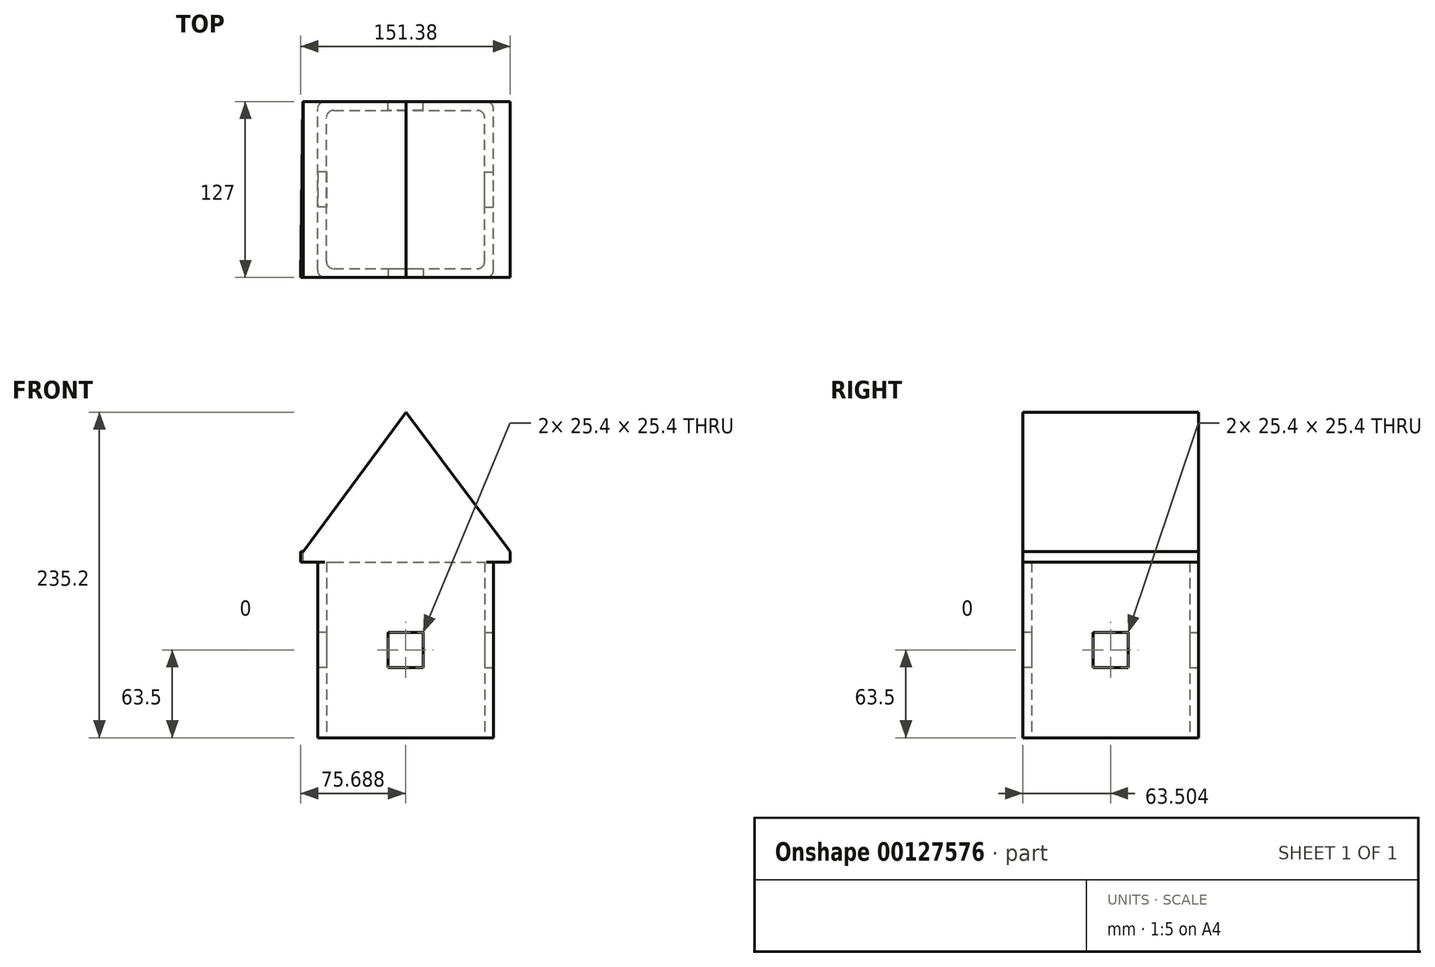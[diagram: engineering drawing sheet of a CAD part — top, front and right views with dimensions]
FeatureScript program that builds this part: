
annotation { "Feature Type Name" : "Feature", "Feature Type Description" : "" }
export const myFeature = defineFeature(function(context is Context, id is Id, definition is map)
    precondition{}
    {
        {
            var Q0;
            Q0=qCreatedBy(makeId("Top.planeOp"),FACE);
            var sketch = newSketch(context, id + "F0", { "sketchPlane" : qUnion([Q0])});
            skLineSegment(sketch, "E0.bottom", {"start": v(-63.96, -29.64) * mm, "end": v(63.04, -29.64) * mm});
            skLineSegment(sketch, "E0.top", {"start": v(-63.96, 97.36) * mm, "end": v(63.04, 97.36) * mm});
            skLineSegment(sketch, "E0.left", {"start": v(-63.96, -29.64) * mm, "end": v(-63.96, 97.36) * mm});
            skLineSegment(sketch, "E0.right", {"start": v(63.04, -29.64) * mm, "end": v(63.04, 97.36) * mm});
            skLineSegment(sketch, "E1.0", {"start": v(-57.61, 91.01) * mm, "end": v(56.69, 91.01) * mm});
            skLineSegment(sketch, "E1.1", {"start": v(-57.61, -23.29) * mm, "end": v(-57.61, 91.01) * mm});
            skLineSegment(sketch, "E1.2", {"start": v(-57.61, -23.29) * mm, "end": v(56.69, -23.29) * mm});
            skLineSegment(sketch, "E1.3", {"start": v(56.69, -23.29) * mm, "end": v(56.69, 91.01) * mm});
            skSolve(sketch);
        }
        {
            var Q0;
            Q0=makeQuery(id+"F0.imprint","IMPRINT",FACE,{"disambiguationData":[TD([[makeQuery(id+"F0.imprint","IMPRINT",EDGE,{"derivedFrom":sQuery(id+"F0.wireOp",EDGE,"E0.bottom")}),1.0]])]});
            extrude(context, id + "F1", {"entities" : qUnion([Q0]), "depth" : 127 * mm});
        }
        {
            var Q0;
            Q0=makeQuery(id+"F1.opExtrude","SWEPT_FACE",FACE,{"disambiguationData":[OSD([sQuery(id+"F0.wireOp",EDGE,"E0.right")])]});
            var sketch = newSketch(context, id + "F2", { "sketchPlane" : qUnion([Q0])});
            skLineSegment(sketch, "E2.bottom", {"start": v(21.16, 76.2) * mm, "end": v(46.56, 76.2) * mm});
            skLineSegment(sketch, "E2.top", {"start": v(21.16, 50.8) * mm, "end": v(46.56, 50.8) * mm});
            skLineSegment(sketch, "E2.left", {"start": v(21.16, 76.2) * mm, "end": v(21.16, 50.8) * mm});
            skLineSegment(sketch, "E2.right", {"start": v(46.56, 76.2) * mm, "end": v(46.56, 50.8) * mm});
            skSolve(sketch);
        }
        {
            var Q0;
            Q0=makeQuery(id+"F2.imprint","IMPRINT",FACE,{"disambiguationData":[TD([[makeQuery(id+"F2.imprint","IMPRINT",EDGE,{"derivedFrom":sQuery(id+"F2.wireOp",EDGE,"E2.bottom")}),-1.0]])]});
            var Q1;
            Q1=makeQuery(id+"F1.opExtrude","SWEPT_FACE",FACE,{"disambiguationData":[OSD([sQuery(id+"F0.wireOp",EDGE,"E1.3")])]});
            extrude(context, id + "F3", {"entities" : qUnion([Q0]), "operationType" : NewBodyOperationType.REMOVE, "endBound" : BoundingType.UP_TO_SURFACE, "oppositeDirection" : true, "endBoundEntityFace" : qUnion([Q1]), "depth" : 6.35 * mm});
        }
        {
            var Q0;
            Q0=makeQuery(id+"F1.opExtrude","SWEPT_FACE",FACE,{"disambiguationData":[OSD([sQuery(id+"F0.wireOp",EDGE,"E0.right")])]});
            var Q1;
            Q1=makeQuery(id+"F1.opExtrude","SWEPT_FACE",FACE,{"disambiguationData":[OSD([sQuery(id+"F0.wireOp",EDGE,"E0.left")])]});
            cPlane(context, id + "F4", {"entities" : qUnion([Q0, Q1]), "cplaneType" : CPlaneType.MID_PLANE, "offset" : 25.4 * mm, "width" : 152.4 * mm, "height" : 152.4 * mm});
        }
        {
            var Q0;
            Q0=qCreatedBy(id+"F4.planeOp",FACE);
            var sketch = newSketch(context, id + "F5", { "sketchPlane" : qUnion([Q0])});
            skLineSegment(sketch, "E3.0", {"start": v(-29.64, 127) * mm, "end": v(97.36, 127) * mm});
            skLineSegment(sketch, "E4", {"start": v(33.86, 127) * mm, "end": v(33.86, 29.75) * mm});
            skSolve(sketch);
        }
        {
            var Q0;
            Q0=makeQuery(id+"F3.boolean.opBoolean","COPY",FACE,{"derivedFrom":makeQuery(id+"F3.opExtrude","SWEPT_FACE",FACE,{"disambiguationData":[OSD([sQuery(id+"F2.wireOp",EDGE,"E2.left")])]})});
            var Q1;
            Q1=makeQuery(id+"F3.boolean.opBoolean","COPY",FACE,{"derivedFrom":makeQuery(id+"F3.opExtrude","SWEPT_FACE",FACE,{"disambiguationData":[OSD([sQuery(id+"F2.wireOp",EDGE,"E2.right")])]})});
            var Q2;
            Q2=makeQuery(id+"F3.boolean.opBoolean","COPY",FACE,{"derivedFrom":makeQuery(id+"F3.opExtrude","SWEPT_FACE",FACE,{"disambiguationData":[OSD([sQuery(id+"F2.wireOp",EDGE,"E2.bottom")])]})});
            var Q3;
            Q3=makeQuery(id+"F3.boolean.opBoolean","COPY",FACE,{"derivedFrom":makeQuery(id+"F3.opExtrude","SWEPT_FACE",FACE,{"disambiguationData":[OSD([sQuery(id+"F2.wireOp",EDGE,"E2.top")])]})});
            var Q4;
            Q4=sQuery(id+"F5.wireOp",EDGE,"E4");
            circularPattern(context, id + "F6", {"patternType" : PatternType.FACE, "faces" : qUnion([Q0, Q1, Q2, Q3]), "axis" : qUnion([Q4]), "angle" : 360 * degree, "instanceCount" : 4, "equalSpace" : true});
        }
        {
            var Q0;
            Q0=makeQuery(id+"F1.opExtrude","SWEPT_EDGE",EDGE,{"disambiguationData":[OSD([sQuery(id+"F0.wireOp",EDGE,"E0.bottom"),sQuery(id+"F0.wireOp",EDGE,"E0.left")])]});
            var Q1;
            Q1=makeQuery(id+"F1.opExtrude","SWEPT_EDGE",EDGE,{"disambiguationData":[OSD([sQuery(id+"F0.wireOp",EDGE,"E0.bottom"),sQuery(id+"F0.wireOp",EDGE,"E0.right")])]});
            var Q2;
            Q2=makeQuery(id+"F1.opExtrude","SWEPT_EDGE",EDGE,{"disambiguationData":[OSD([sQuery(id+"F0.wireOp",EDGE,"E0.top"),sQuery(id+"F0.wireOp",EDGE,"E0.left")])]});
            var Q3;
            Q3=makeQuery(id+"F1.opExtrude","SWEPT_EDGE",EDGE,{"disambiguationData":[OSD([sQuery(id+"F0.wireOp",EDGE,"E1.0"),sQuery(id+"F0.wireOp",EDGE,"E1.3")])]});
            var Q4;
            Q4=makeQuery(id+"F1.opExtrude","SWEPT_EDGE",EDGE,{"disambiguationData":[OSD([sQuery(id+"F0.wireOp",EDGE,"E0.top"),sQuery(id+"F0.wireOp",EDGE,"E0.right")])]});
            var Q5;
            Q5=makeQuery(id+"F1.opExtrude","SWEPT_EDGE",EDGE,{"disambiguationData":[OSD([sQuery(id+"F0.wireOp",EDGE,"E1.0"),sQuery(id+"F0.wireOp",EDGE,"E1.1")])]});
            var Q6;
            Q6=makeQuery(id+"F1.opExtrude","SWEPT_EDGE",EDGE,{"disambiguationData":[OSD([sQuery(id+"F0.wireOp",EDGE,"E1.1"),sQuery(id+"F0.wireOp",EDGE,"E1.2")])]});
            var Q7;
            Q7=makeQuery(id+"F1.opExtrude","SWEPT_EDGE",EDGE,{"disambiguationData":[OSD([sQuery(id+"F0.wireOp",EDGE,"E1.2"),sQuery(id+"F0.wireOp",EDGE,"E1.3")])]});
            fillet(context, id + "F7", {"entities" : qUnion([Q0, Q1, Q2, Q3, Q4, Q5, Q6, Q7]), "radius" : 5.08 * mm, "tangentPropagation" : true, "allowEdgeOverflow" : false});
        }
        {
            var Q0;
            Q0=makeQuery(id+"F1.opExtrude","CAP_FACE",FACE,{"disambiguationData":[OSD([sQuery(id+"F0.wireOp",EDGE,"E0.bottom"),sQuery(id+"F0.wireOp",EDGE,"E0.top"),sQuery(id+"F0.wireOp",EDGE,"E0.left"),sQuery(id+"F0.wireOp",EDGE,"E0.right"),sQuery(id+"F0.wireOp",EDGE,"E1.0"),sQuery(id+"F0.wireOp",EDGE,"E1.1"),sQuery(id+"F0.wireOp",EDGE,"E1.2"),sQuery(id+"F0.wireOp",EDGE,"E1.3")])],"isStart":false});
            var sketch = newSketch(context, id + "F8", { "sketchPlane" : qUnion([Q0])});
            skLineSegment(sketch, "E5.0", {"start": v(-76.15, -29.64) * mm, "end": v(75.23, -29.64) * mm});
            skLineSegment(sketch, "E6.0", {"start": v(63.04, -24.56) * mm, "end": v(63.04, 92.28) * mm});
            skLineSegment(sketch, "E7.0", {"start": v(-63.96, -24.56) * mm, "end": v(-63.96, 92.28) * mm});
            skLineSegment(sketch, "E8.0", {"start": v(-74.8, 97.36) * mm, "end": v(75.23, 97.36) * mm});
            skLineSegment(sketch, "E9", {"start": v(75.23, -35.33) * mm, "end": v(75.23, 108.3) * mm});
            skLineSegment(sketch, "E10", {"start": v(-0.46, -29.64) * mm, "end": v(0, 56.91) * mm, "construction": true});
            skLineSegment(sketch, "E11.MirrorCS", {"start": v(-76.2, -34.52) * mm, "end": v(-74.67, 109.1) * mm});
            skPoint(sketch, "E12.orphan", {"position": v(57.96, -29.64) * mm});
            skPoint(sketch, "E13.orphan", {"position": v(57.96, 97.36) * mm});
            skPoint(sketch, "E14.orphan", {"position": v(-58.88, 97.36) * mm});
            skPoint(sketch, "E15.orphan", {"position": v(-58.88, -29.64) * mm});
            skSolve(sketch);
        }
        {
            var Q0;
            Q0=makeQuery(id+"F8.imprint","IMPRINT",FACE,{"disambiguationData":[TD([[makeQuery(id+"F8.imprint","IMPRINT",EDGE,{"derivedFrom":sQuery(id+"F8.wireOp",EDGE,"E6.0")}),-1.0]])]});
            var Q1;
            Q1=makeQuery(id+"F8.imprint","IMPRINT",FACE,{"disambiguationData":[TD([[makeQuery(id+"F8.imprint","IMPRINT",EDGE,{"derivedFrom":sQuery(id+"F8.wireOp",EDGE,"E6.0")}),1.0]])]});
            var Q2;
            {var subQ3=sQuery(id+"F0.wireOp",EDGE,"E1.0");Q2=makeQuery(id+"F8.imprint","IMPRINT",FACE,{"disambiguationData":[TD([[makeQuery(id+"F8.imprint","IMPRINT",EDGE,{"derivedFrom":makeQuery(id+"F1.opExtrude","CAP_EDGE",EDGE,{"disambiguationData":[OSD([subQ3])],"isStart":false})}),-1.0]])]});}
            var Q3;
            Q3=makeQuery(id+"F8.imprint","IMPRINT",FACE,{"disambiguationData":[TD([[makeQuery(id+"F8.imprint","IMPRINT",EDGE,{"derivedFrom":sQuery(id+"F8.wireOp",EDGE,"E7.0")}),1.0]])]});
            extrude(context, id + "F9", {"entities" : qUnion([Q0, Q1, Q2, Q3]), "operationType" : NewBodyOperationType.ADD, "depth" : 7.62 * mm});
        }
        {
            var Q0;
            Q0=makeQuery(id+"F9.boolean.opBoolean","MERGE",FACE,{"derivedFrom":[makeQuery(id+"F1.opExtrude","SWEPT_FACE",FACE,{"disambiguationData":[OSD([sQuery(id+"F0.wireOp",EDGE,"E0.top")])]}),makeQuery(id+"F9.opExtrude","SWEPT_FACE",FACE,{"disambiguationData":[OSD([sQuery(id+"F8.wireOp",EDGE,"E8.0")])]})]});
            var sketch = newSketch(context, id + "F10", { "sketchPlane" : qUnion([Q0])});
            skLineSegment(sketch, "E16.0", {"start": v(74.8, 134.62) * mm, "end": v(-75.23, 134.62) * mm, "construction": true});
            skLineSegment(sketch, "E17", {"start": v(-0.21, 134.62) * mm, "end": v(0, 191.7) * mm, "construction": true});
            skLineSegment(sketch, "E18", {"start": v(-75.23, 134.62) * mm, "end": v(13.1, 252.45) * mm});
            skLineSegment(sketch, "E19.MirrorCS", {"start": v(74.8, 134.06) * mm, "end": v(-12.64, 252.55) * mm});
            skSolve(sketch);
        }
        {
            var Q0;
            {var subQ0=sQuery(id+"F10.wireOp",EDGE,"E18");var subQ4=sQuery(id+"F10.wireOp",EDGE,"E19.MirrorCS");var subQ5=makeQuery(id+"F10.imprint","INTERSECT",VERTEX,{"derivedFrom":[subQ0,subQ4]});Q0=makeQuery(id+"F10.imprint","IMPRINT",FACE,{"disambiguationData":[TD([[makeQuery(id+"F10.imprint","IMPRINT",EDGE,{"disambiguationData":[TD([[subQ5,1.0]])],"derivedFrom":subQ4}),1.0]])]});}
            var Q1;
            Q1=makeQuery(id+"F9.boolean.opBoolean","MERGE",FACE,{"derivedFrom":[makeQuery(id+"F1.opExtrude","SWEPT_FACE",FACE,{"disambiguationData":[OSD([sQuery(id+"F0.wireOp",EDGE,"E0.bottom")])]}),makeQuery(id+"F9.opExtrude","SWEPT_FACE",FACE,{"disambiguationData":[OSD([sQuery(id+"F8.wireOp",EDGE,"E5.0")])]})]});
            extrude(context, id + "F11", {"entities" : qUnion([Q0]), "operationType" : NewBodyOperationType.ADD, "endBound" : BoundingType.UP_TO_SURFACE, "oppositeDirection" : true, "endBoundEntityFace" : qUnion([Q1]), "depth" : 25.4 * mm});
        }
    });
